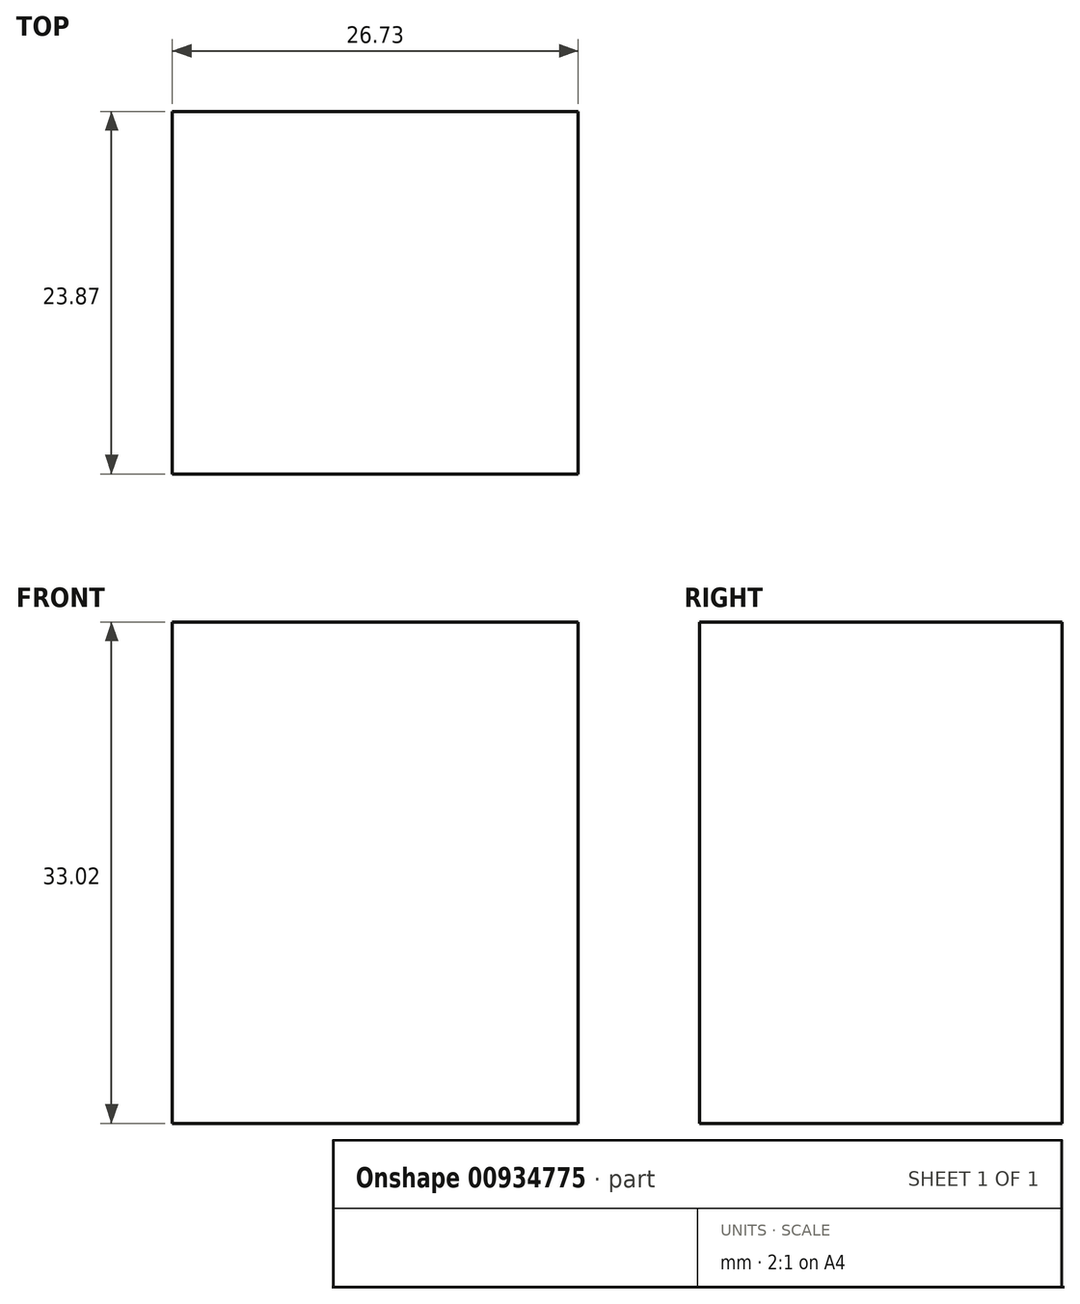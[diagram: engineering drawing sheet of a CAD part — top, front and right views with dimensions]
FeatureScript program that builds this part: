
annotation { "Feature Type Name" : "Feature", "Feature Type Description" : "" }
export const myFeature = defineFeature(function(context is Context, id is Id, definition is map)
    precondition{}
    {
        {
            var Q0;
            Q0=qCreatedBy(makeId("Top.planeOp"),FACE);
            var sketch = newSketch(context, id + "F0", { "sketchPlane" : qUnion([Q0])});
            skLineSegment(sketch, "E0.bottom", {"start": v(0, 3.23) * mm, "end": v(26.73, 3.23) * mm});
            skLineSegment(sketch, "E0.top", {"start": v(0, 27.1) * mm, "end": v(26.73, 27.1) * mm});
            skLineSegment(sketch, "E0.left", {"start": v(0, 3.23) * mm, "end": v(0, 27.1) * mm});
            skLineSegment(sketch, "E0.right", {"start": v(26.73, 3.23) * mm, "end": v(26.73, 27.1) * mm});
            skSolve(sketch);
        }
        {
            var Q0;
            Q0=makeQuery(id+"F0.imprint","IMPRINT",FACE,{"disambiguationData":[TD([[makeQuery(id+"F0.imprint","IMPRINT",EDGE,{"derivedFrom":sQuery(id+"F0.wireOp",EDGE,"E0.bottom")}),1.0]])]});
            extrude(context, id + "F1", {"entities" : qUnion([Q0]), "depth" : 22.86 * mm, "offsetDistance" : 25.4 * mm, "hasSecondDirection" : true, "secondDirectionOppositeDirection" : true, "secondDirectionDepth" : 10.16 * mm});
        }
    });
